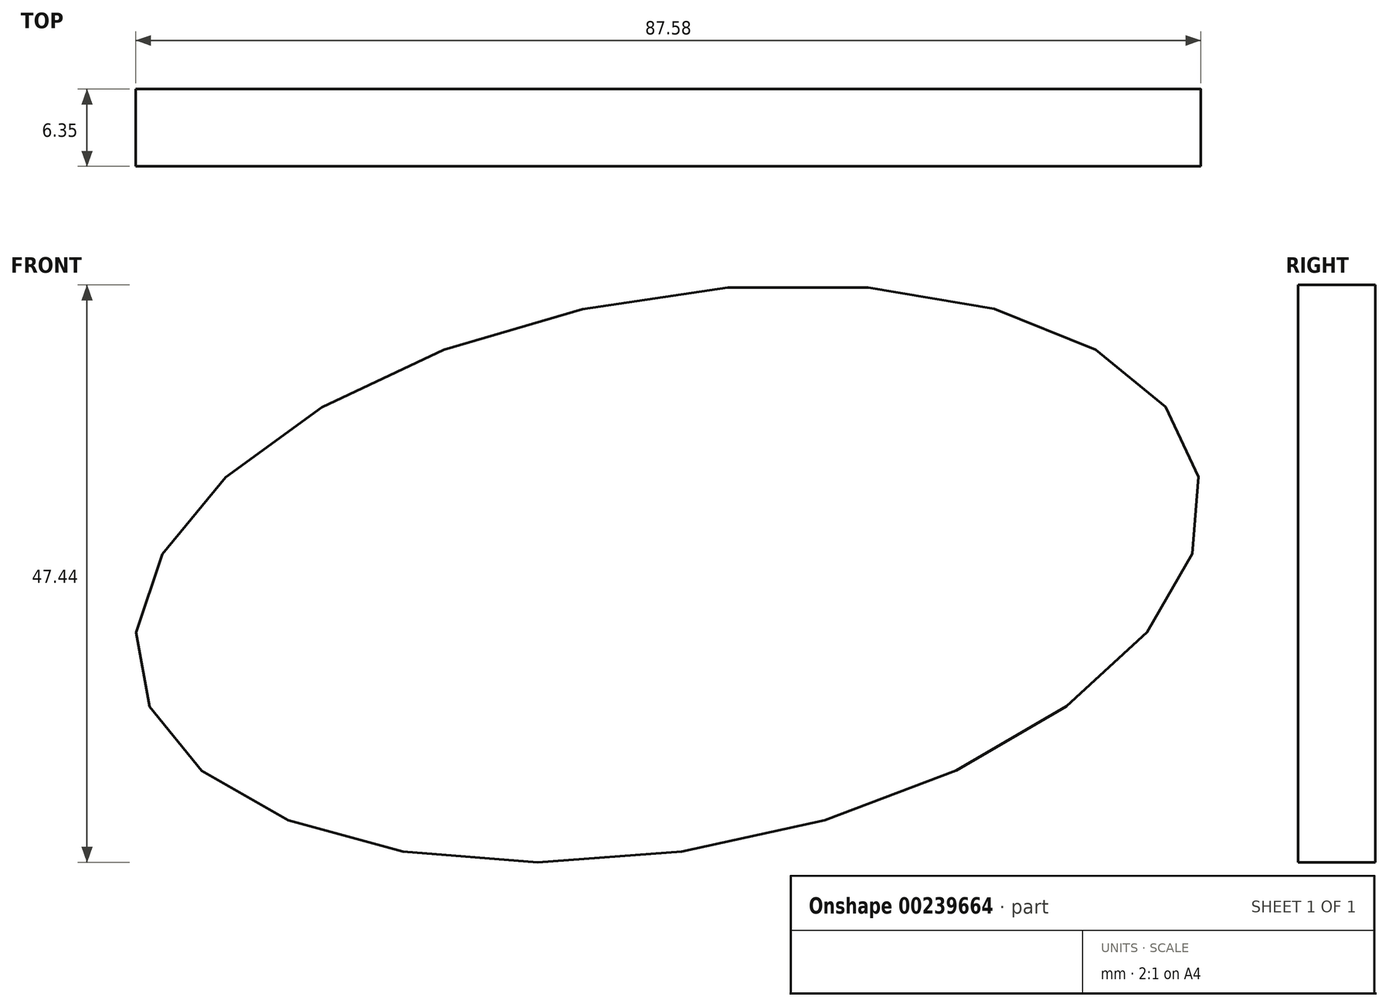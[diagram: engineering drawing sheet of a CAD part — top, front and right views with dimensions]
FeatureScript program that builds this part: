
annotation { "Feature Type Name" : "Feature", "Feature Type Description" : "" }
export const myFeature = defineFeature(function(context is Context, id is Id, definition is map)
    precondition{}
    {
        {
            var Q0;
            Q0=qCreatedBy(makeId("Front.planeOp"),FACE);
            var sketch = newSketch(context, id + "F0", { "sketchPlane" : qUnion([Q0])});
            skEllipse(sketch, "E0", {"center": v(0, 0) * mm, "majorRadius": 44.32 * mm, "minorRadius": 22.71 * mm, "majorAxis": v(0.98, 0.18)});
            skSolve(sketch);
        }
        {
            var Q0;
            Q0=makeQuery(id+"F0.imprint","IMPRINT",FACE,{"disambiguationData":[TD([[makeQuery(id+"F0.imprint","IMPRINT",EDGE,{"derivedFrom":sQuery(id+"F0.wireOp",EDGE,"E0")}),1.0]])]});
            extrude(context, id + "F1", {"entities" : qUnion([Q0]), "depth" : 6.35 * mm});
        }
    });
